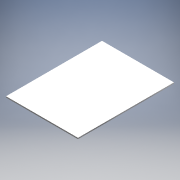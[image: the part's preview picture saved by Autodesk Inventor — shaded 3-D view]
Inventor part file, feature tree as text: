
AUTODESK INVENTOR PART (.ipt)
format: ipt  version: 2019 (Build 230136000, 136)  size: 90,112 bytes
history: native  units: mm
features: extrude x1, sketch x1
ambient origin geometry x8: Origin, YZ Plane, XZ Plane, XY Plane, X Axis, Y Axis, Z Axis, Center Point
bodies: Solid1 (feature_tree)
feature tree (2):
  extrude  "Extrusion1"  Depth=400.0mm
  sketch  "Sketch1"  dims[d0=300.0mm d1=400.0mm d2=5.0mm d3=0.0mm]
